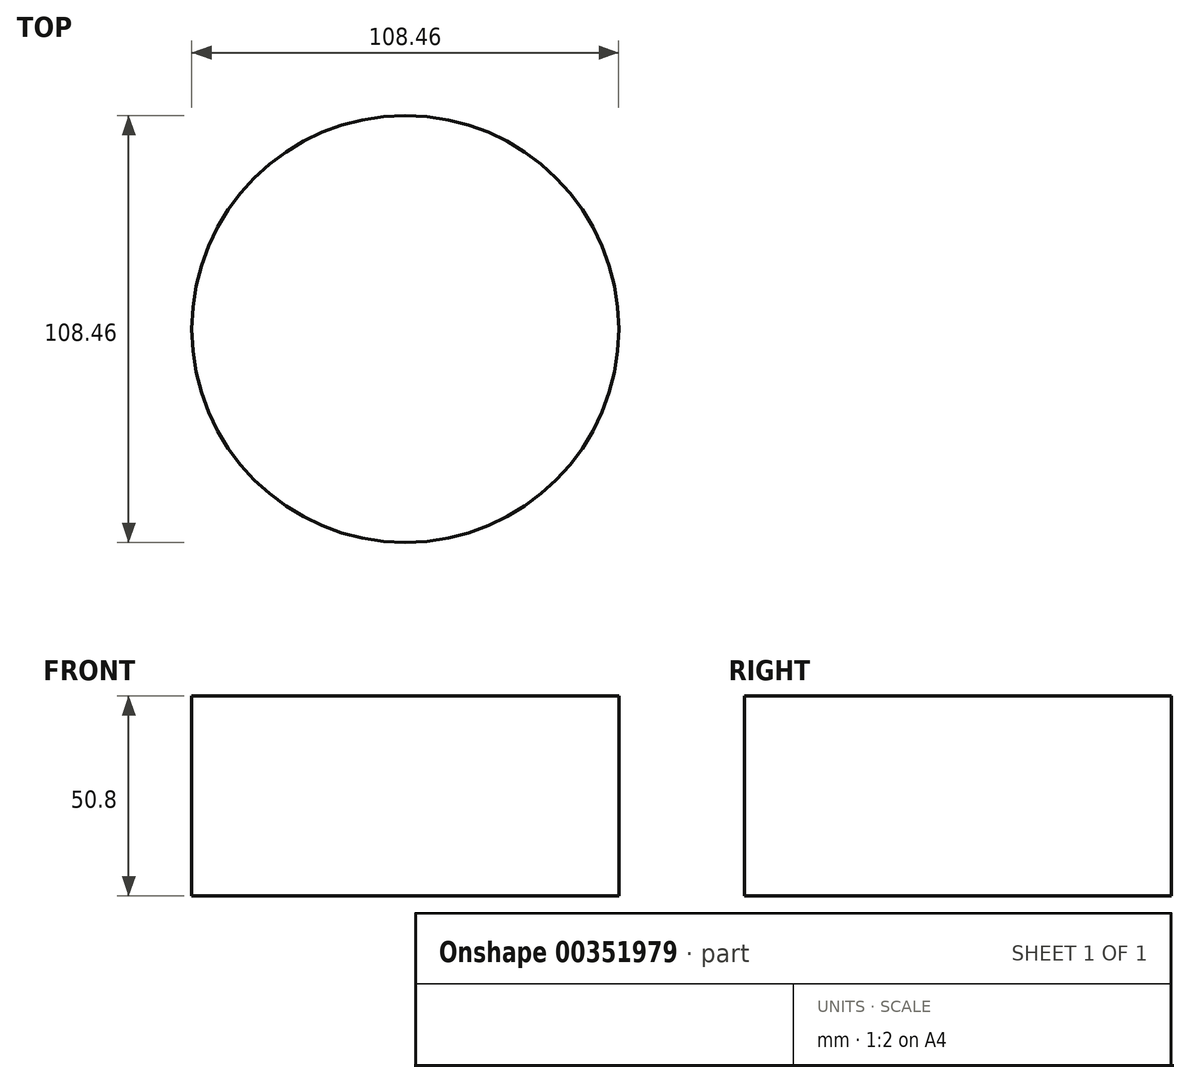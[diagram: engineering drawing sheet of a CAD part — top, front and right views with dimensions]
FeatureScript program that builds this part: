
annotation { "Feature Type Name" : "Feature", "Feature Type Description" : "" }
export const myFeature = defineFeature(function(context is Context, id is Id, definition is map)
    precondition{}
    {
        {
            var Q0;
            Q0=qCreatedBy(makeId("Top.planeOp"),FACE);
            var sketch = newSketch(context, id + "F0", { "sketchPlane" : qUnion([Q0])});
            skCircle(sketch, "E0", {"center": v(0, 0) * mm, "radius": 54.23 * mm});
            skSolve(sketch);
        }
        {
            var Q0;
            Q0 = qSketchRegion(id + "F0", true);
            var Q1;
            Q1=makeQuery(id+"F0.imprint","IMPRINT",FACE,{"disambiguationData":[TD([[makeQuery(id+"F0.imprint","IMPRINT",EDGE,{"derivedFrom":sQuery(id+"F0.wireOp",EDGE,"E0")}),1.0]])]});
            extrude(context, id + "F1", {"entities" : qUnion([Q0, Q1]), "depth" : 50.8 * mm});
        }
    });
